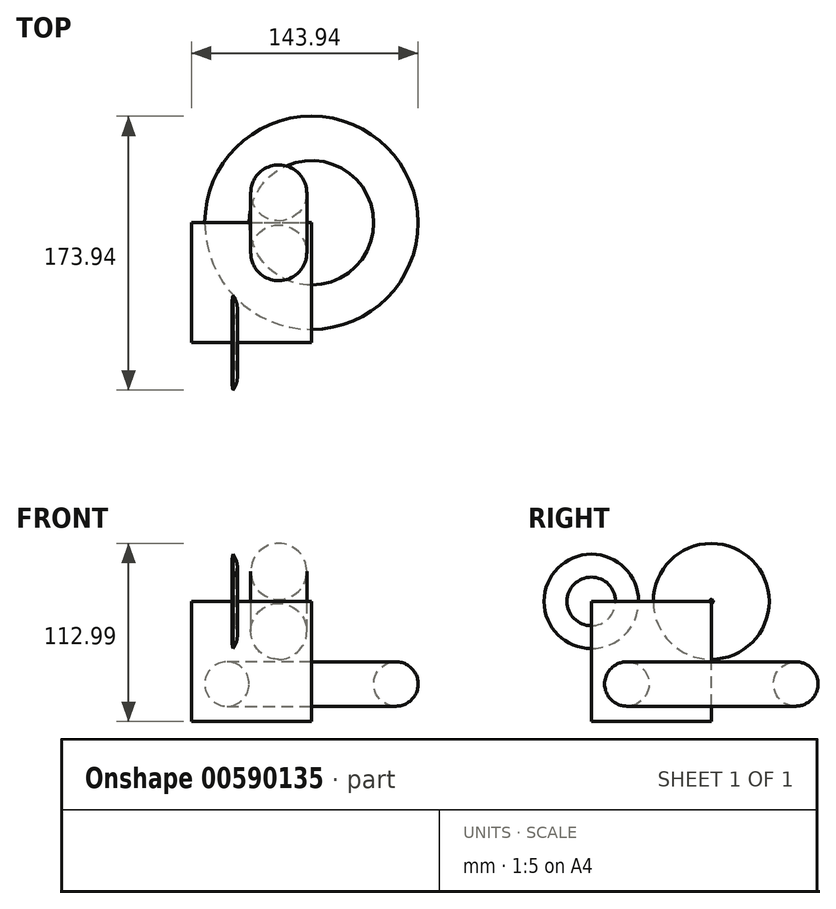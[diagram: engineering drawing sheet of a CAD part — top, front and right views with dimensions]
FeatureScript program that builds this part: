
annotation { "Feature Type Name" : "Feature", "Feature Type Description" : "" }
export const myFeature = defineFeature(function(context is Context, id is Id, definition is map)
    precondition{}
    {
        {
            var Q0;
            Q0=qCreatedBy(makeId("Front.planeOp"),FACE);
            var sketch = newSketch(context, id + "F0", { "sketchPlane" : qUnion([Q0])});
            skLineSegment(sketch, "E0.bottom", {"start": v(0, 0) * mm, "end": v(76.2, 0) * mm});
            skLineSegment(sketch, "E0.top", {"start": v(0, 76.2) * mm, "end": v(76.2, 76.2) * mm});
            skLineSegment(sketch, "E0.left", {"start": v(0, 0) * mm, "end": v(0, 76.2) * mm});
            skLineSegment(sketch, "E0.right", {"start": v(76.2, 0) * mm, "end": v(76.2, 76.2) * mm});
            skSolve(sketch);
        }
        {
            var Q0;
            Q0=makeQuery(id+"F0.imprint","IMPRINT",FACE,{"disambiguationData":[TD([[makeQuery(id+"F0.imprint","IMPRINT",EDGE,{"derivedFrom":sQuery(id+"F0.wireOp",EDGE,"E0.bottom")}),1.0]])]});
            extrude(context, id + "F1", {"entities" : qUnion([Q0]), "depth" : 76.2 * mm, "offsetDistance" : 25.4 * mm});
        }
        {
            var Q0;
            Q0=makeQuery(id+"F1.opExtrude","CAP_FACE",FACE,{"disambiguationData":[OSD([sQuery(id+"F0.wireOp",EDGE,"E0.bottom"),sQuery(id+"F0.wireOp",EDGE,"E0.top"),sQuery(id+"F0.wireOp",EDGE,"E0.left"),sQuery(id+"F0.wireOp",EDGE,"E0.right")])],"isStart":false});
            var sketch = newSketch(context, id + "F2", { "sketchPlane" : qUnion([Q0])});
            skCircle(sketch, "E1", {"center": v(15.8, 54.33) * mm, "radius": 13.33 * mm});
            skSolve(sketch);
        }
        {
            var Q0;
            Q0 = qSketchRegion(id + "F2", true);
            var Q1;
            Q1=makeQuery(id+"F1.opExtrude","CAP_EDGE",EDGE,{"disambiguationData":[OSD([sQuery(id+"F0.wireOp",EDGE,"E0.top")])],"isStart":false});
            revolve(context, id + "F3", {"entities" : qUnion([Q0]), "axis" : qUnion([Q1]), "revolveType" : RevolveType.FULL});
        }
        {
            var Q0;
            Q0=makeQuery(id+"F1.opExtrude","CAP_FACE",FACE,{"disambiguationData":[OSD([sQuery(id+"F0.wireOp",EDGE,"E0.bottom"),sQuery(id+"F0.wireOp",EDGE,"E0.top"),sQuery(id+"F0.wireOp",EDGE,"E0.left"),sQuery(id+"F0.wireOp",EDGE,"E0.right")])],"isStart":true});
            var sketch = newSketch(context, id + "F4", { "sketchPlane" : qUnion([Q0])});
            skCircle(sketch, "E2", {"center": v(-55.45, 57.19) * mm, "radius": 17.78 * mm});
            skSolve(sketch);
        }
        {
            var Q0;
            Q0=makeQuery(id+"F4.imprint","IMPRINT",FACE,{"disambiguationData":[TD([[makeQuery(id+"F4.imprint","IMPRINT",EDGE,{"derivedFrom":sQuery(id+"F4.wireOp",EDGE,"E2")}),1.0]])]});
            var Q1;
            Q1=makeQuery(id+"F1.opExtrude","CAP_EDGE",EDGE,{"disambiguationData":[OSD([sQuery(id+"F0.wireOp",EDGE,"E0.top")])],"isStart":true});
            revolve(context, id + "F5", {"entities" : qUnion([Q0]), "axis" : qUnion([Q1]), "revolveType" : RevolveType.FULL});
        }
        {
            var Q0;
            Q0=makeQuery(id+"F1.opExtrude","CAP_FACE",FACE,{"disambiguationData":[OSD([sQuery(id+"F0.wireOp",EDGE,"E0.bottom"),sQuery(id+"F0.wireOp",EDGE,"E0.top"),sQuery(id+"F0.wireOp",EDGE,"E0.left"),sQuery(id+"F0.wireOp",EDGE,"E0.right")])],"isStart":false});
            var sketch = newSketch(context, id + "F6", { "sketchPlane" : qUnion([Q0])});
            skCircle(sketch, "E3", {"center": v(48.52, 51.85) * mm, "radius": 22.86 * mm});
            skSolve(sketch);
        }
        {
            var Q0;
            Q0=makeQuery(id+"F6.imprint","IMPRINT",FACE,{"disambiguationData":[TD([[makeQuery(id+"F6.imprint","IMPRINT",EDGE,{"derivedFrom":sQuery(id+"F6.wireOp",EDGE,"E3")}),1.0]])]});
            var Q1;
            Q1=makeQuery(id+"F1.opExtrude","CAP_EDGE",EDGE,{"disambiguationData":[OSD([sQuery(id+"F0.wireOp",EDGE,"E0.top")])],"isStart":false});
            revolve(context, id + "F7", {"entities" : qUnion([Q0]), "axis" : qUnion([Q1]), "revolveType" : RevolveType.FULL});
        }
        {
            var Q0;
            Q0=makeQuery(id+"F7.opRevolve","SWEPT_BODY",BODY,{"disambiguationData":[OSD([sQuery(id+"F6.wireOp",EDGE,"E3")])]});
            var Q1;
            Q1=makeQuery(id+"F3.opRevolve","SWEPT_BODY",BODY,{"disambiguationData":[OSD([sQuery(id+"F2.wireOp",EDGE,"E1")])]});
            var Q2;
            Q2=makeQuery(id+"F5.opRevolve","SWEPT_BODY",BODY,{"disambiguationData":[OSD([sQuery(id+"F4.wireOp",EDGE,"E2")])]});
            booleanBodies(context, id + "F8", {"operationType" : BooleanOperationType.INTERSECTION, "tools" : qUnion([Q0, Q1]), "targets" : qUnion([Q2])});
        }
        {
            var Q0;
            Q0=makeQuery(id+"F1.opExtrude","SWEPT_FACE",FACE,{"disambiguationData":[OSD([sQuery(id+"F0.wireOp",EDGE,"E0.right")])]});
            var sketch = newSketch(context, id + "F9", { "sketchPlane" : qUnion([Q0])});
            skCircle(sketch, "E4", {"center": v(-53.65, 23.75) * mm, "radius": 14.1 * mm});
            skSolve(sketch);
        }
        {
            var Q0;
            Q0=makeQuery(id+"F9.imprint","IMPRINT",FACE,{"disambiguationData":[TD([[makeQuery(id+"F9.imprint","IMPRINT",EDGE,{"derivedFrom":sQuery(id+"F9.wireOp",EDGE,"E4")}),1.0]])]});
            var Q1;
            Q1=makeQuery(id+"F1.opExtrude","CAP_EDGE",EDGE,{"disambiguationData":[OSD([sQuery(id+"F0.wireOp",EDGE,"E0.right")])],"isStart":true});
            revolve(context, id + "F10", {"entities" : qUnion([Q0]), "axis" : qUnion([Q1]), "revolveType" : RevolveType.FULL});
        }
    });
